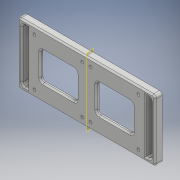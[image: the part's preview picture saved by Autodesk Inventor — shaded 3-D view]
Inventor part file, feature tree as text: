
AUTODESK INVENTOR PART (.ipt)
format: ipt  version: 2017 (Build 210142000, 142)  size: 280,064 bytes
history: native  units: mm
features: sketch x6, extrude x5, fillet x3, mirror x2, chamfer x2, projected_geometry x2, hole x1
ambient origin geometry x8: Origin, YZ Plane, XZ Plane, XY Plane, X Axis, Y Axis, Z Axis, Center Point
bodies: Solid1 (feature_tree)
feature tree (21):
  extrude  "Extrusion1"  Depth=98.0mm
  extrude  "Extrusion2"  Depth=40.0mm
  extrude  "Extrusion3"  TaperAngle=0.0deg  [1 undecoded]
  extrude  "Extrusion4"  Depth=6.0mm
  fillet  "Fillet1"  Radius=6.0mm
  extrude  "Extrusion5"  Depth=6.0mm
  fillet  "Fillet2"  Radius=6.0mm
  mirror  "Mirror1"
  fillet  "Fillet3"  Radius=6.0mm
  chamfer  "Chamfer1"  Distance=2.0mm
  chamfer  "Chamfer2"  Distance=26.0mm
  hole  "Hole1"  [1 undecoded]
  mirror  "Mirror2"
  sketch  "Sketch1"  dims[d0=44.0mm d1=98.0mm]
  sketch  "Sketch2"  dims[d2=5.0mm d3=0.0mm d4=40.0mm]
  sketch  "Sketch3"  dims[d5=40.0mm d6=0.0mm]
  projected_geometry  "Projected Loop1"
  sketch  "Sketch4"  dims[d7=3.0mm d8=0.0mm d9=6.0mm d10=6.0mm]
  projected_geometry  "Projected Loop2"
  sketch  "Sketch5"  dims[d11=6.0mm d12=6.0mm d13=6.0mm d14=6.0mm]
  sketch  "Sketch6"  dims[d15=6.0mm d16=2.0mm d17=0.0mm d18=26.0mm d19=20.0mm d20=20.0mm d21=20.0mm d22=2.0mm d23=0.0mm d24=2.0mm d25=38.0mm d26=2.0mm d27=4.0mm d28=2.0mm d29=0.0mm d30=2.0mm d31=2.0mm d32=1.0mm d33=2.0mm d34=45.0deg d35=1.0mm d36=2.0mm d37=45.0deg d38=6.0mm d39=34.0mm d40=34.0mm d41=20.0mm d42=2.0mm d43=6.0mm d44=4.0mm d45=2.0mm d46=90.0deg d47=8.0mm d48=20.594885mm]
note: 2 required parameter values undecoded (feature->parameter linkage not recoverable at this tier; creation-order binding heuristic only, values carry confidence <= 0.55)
